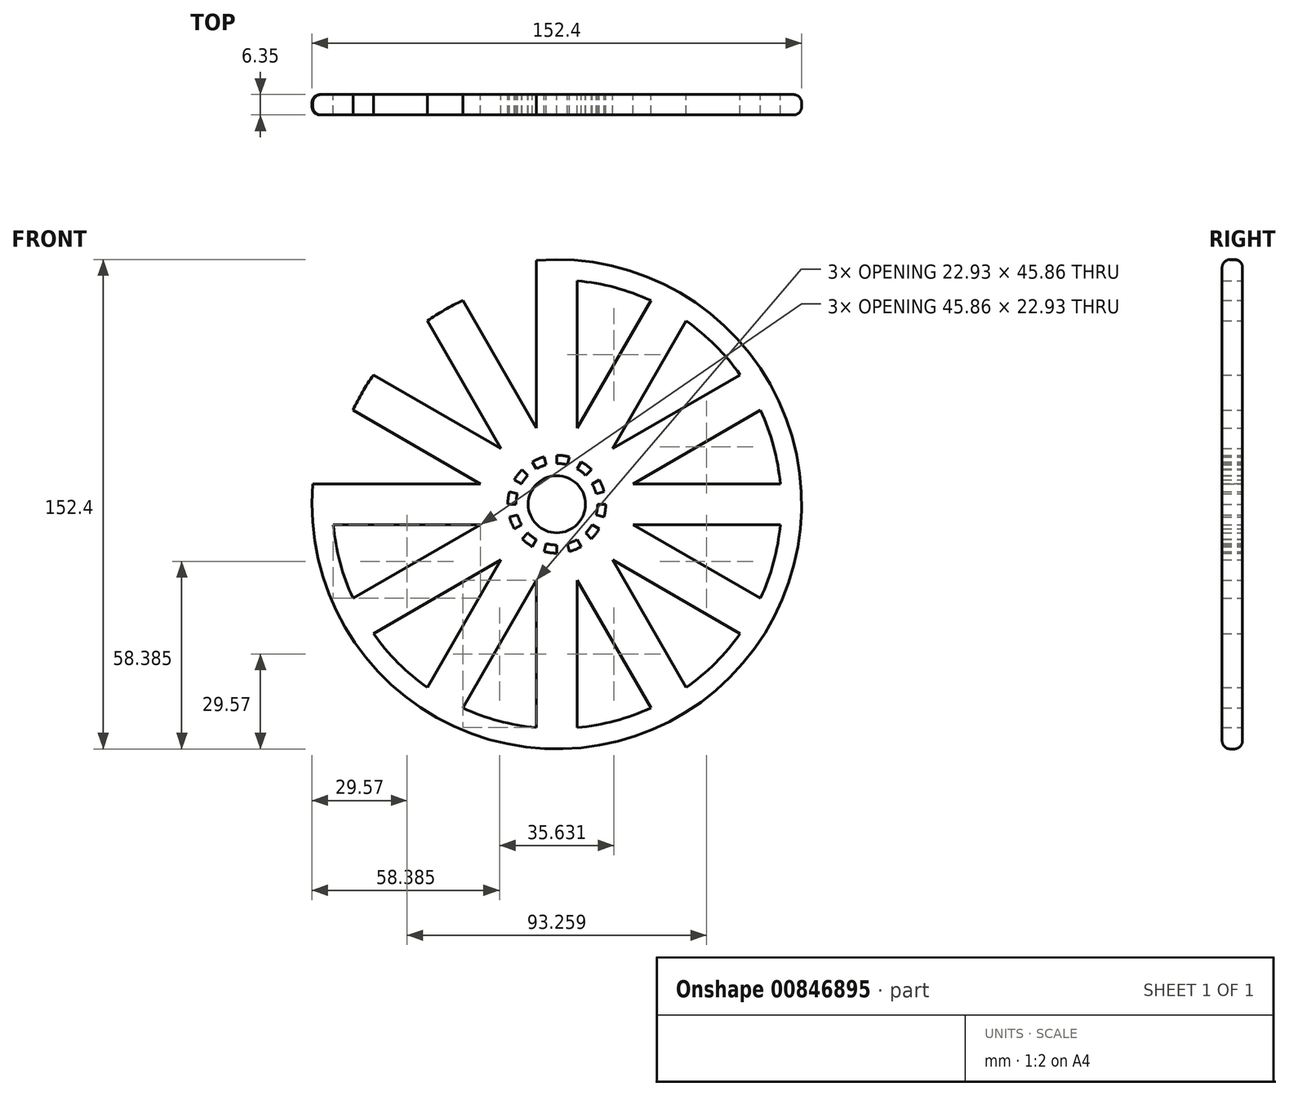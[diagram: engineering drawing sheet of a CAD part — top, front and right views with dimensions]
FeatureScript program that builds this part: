
annotation { "Feature Type Name" : "Feature", "Feature Type Description" : "" }
export const myFeature = defineFeature(function(context is Context, id is Id, definition is map)
    precondition{}
    {
        {
            var Q0;
            Q0=qCreatedBy(makeId("Front.planeOp"),FACE);
            var sketch = newSketch(context, id + "F0", { "sketchPlane" : qUnion([Q0])});
            skCircle(sketch, "E0", {"center": v(0, 0) * mm, "radius": 76.2 * mm});
            skLineSegment(sketch, "E1", {"start": v(-76.2, 0) * mm, "end": v(0, 0) * mm});
            skLineSegment(sketch, "E2", {"start": v(0, 0) * mm, "end": v(76.2, 0) * mm});
            skLineSegment(sketch, "E3", {"start": v(76.2, 0) * mm, "end": v(0, 0) * mm});
            skLineSegment(sketch, "E4", {"start": v(0, 0) * mm, "end": v(0, 76.2) * mm});
            skLineSegment(sketch, "E5", {"start": v(0, 76.2) * mm, "end": v(0, 0) * mm});
            skLineSegment(sketch, "E6", {"start": v(0, 0) * mm, "end": v(0, -76.2) * mm});
            skLineSegment(sketch, "E7", {"start": v(0, -76.2) * mm, "end": v(0, 0) * mm});
            skArc(sketch, "E8", {"start": v(-76.2, 0) * mm, "mid": v(-53.88, 53.88) * mm, "end": v(0, 76.2) * mm});
            skArc(sketch, "E9", {"start": v(76.2, 0) * mm, "mid": v(53.88, 53.88) * mm, "end": v(0, 76.2) * mm});
            skArc(sketch, "E10", {"start": v(-76.2, 0) * mm, "mid": v(-53.88, -53.88) * mm, "end": v(0, -76.2) * mm});
            skArc(sketch, "E11", {"start": v(0, -76.2) * mm, "mid": v(53.88, -53.88) * mm, "end": v(76.2, 0) * mm});
            skLineSegment(sketch, "E12", {"start": v(0, 0) * mm, "end": v(0, 6.35) * mm});
            skLineSegment(sketch, "E13", {"start": v(0, 0) * mm, "end": v(-6.35, 0) * mm});
            skLineSegment(sketch, "E14", {"start": v(0, 0) * mm, "end": v(66, 38.1) * mm});
            skLineSegment(sketch, "E15", {"start": v(0, 0) * mm, "end": v(38.1, 66) * mm});
            skLineSegment(sketch, "E16.MirrorCS", {"start": v(0, 0) * mm, "end": v(-38.1, 66) * mm});
            skLineSegment(sketch, "E17.MirrorCS", {"start": v(0, 0) * mm, "end": v(-66, 38.1) * mm});
            skLineSegment(sketch, "E18.MirrorCS", {"start": v(0, 0) * mm, "end": v(-66, -38.1) * mm});
            skLineSegment(sketch, "E19.MirrorCS", {"start": v(0, 0) * mm, "end": v(-38.1, -66) * mm});
            skLineSegment(sketch, "E20.MirrorCS", {"start": v(0, 0) * mm, "end": v(38.1, -66) * mm});
            skLineSegment(sketch, "E21.MirrorCS", {"start": v(0, 0) * mm, "end": v(66, -38.1) * mm});
            skArc(sketch, "E22.0", {"start": v(-69.85, 0) * mm, "mid": v(-49.4, 49.4) * mm, "end": v(0, 69.85) * mm});
            skArc(sketch, "E23.MirrorCS", {"start": v(69.85, 0) * mm, "mid": v(49.4, 49.4) * mm, "end": v(0, 69.85) * mm});
            skArc(sketch, "E24.MirrorCS", {"start": v(-69.85, 0) * mm, "mid": v(-49.4, -49.4) * mm, "end": v(0, -69.85) * mm});
            skArc(sketch, "E25.MirrorCS", {"start": v(69.85, 0) * mm, "mid": v(49.4, -49.4) * mm, "end": v(0, -69.85) * mm});
            skLineSegment(sketch, "E26.0", {"start": v(-23.7, 6.35) * mm, "end": v(-69.17, 32.6) * mm});
            skLineSegment(sketch, "E26.1", {"start": v(-76.2, 6.35) * mm, "end": v(-23.7, 6.35) * mm});
            skLineSegment(sketch, "E27.0", {"start": v(-17.35, 17.35) * mm, "end": v(-62.82, 43.6) * mm});
            skLineSegment(sketch, "E27.1", {"start": v(-17.35, 17.35) * mm, "end": v(-43.6, 62.82) * mm});
            skLineSegment(sketch, "E28.0", {"start": v(-6.35, 23.7) * mm, "end": v(-32.6, 69.17) * mm});
            skLineSegment(sketch, "E28.1", {"start": v(-6.35, 76.2) * mm, "end": v(-6.35, 23.7) * mm});
            skLineSegment(sketch, "E29.0", {"start": v(6.35, 23.7) * mm, "end": v(32.6, 69.17) * mm});
            skLineSegment(sketch, "E29.1", {"start": v(6.35, 76.2) * mm, "end": v(6.35, 23.7) * mm});
            skLineSegment(sketch, "E30.0", {"start": v(17.35, 17.35) * mm, "end": v(43.6, 62.82) * mm});
            skLineSegment(sketch, "E30.1", {"start": v(17.35, 17.35) * mm, "end": v(62.82, 43.6) * mm});
            skLineSegment(sketch, "E31.0", {"start": v(23.7, 6.35) * mm, "end": v(69.17, 32.6) * mm});
            skLineSegment(sketch, "E31.1", {"start": v(76.2, 6.35) * mm, "end": v(23.7, 6.35) * mm});
            skLineSegment(sketch, "E32.0", {"start": v(23.7, -6.35) * mm, "end": v(69.17, -32.6) * mm});
            skLineSegment(sketch, "E32.1", {"start": v(76.2, -6.35) * mm, "end": v(23.7, -6.35) * mm});
            skLineSegment(sketch, "E33.0", {"start": v(17.35, -17.35) * mm, "end": v(62.82, -43.6) * mm});
            skLineSegment(sketch, "E33.1", {"start": v(17.35, -17.35) * mm, "end": v(43.6, -62.82) * mm});
            skLineSegment(sketch, "E34.0", {"start": v(6.35, -23.7) * mm, "end": v(32.6, -69.17) * mm});
            skLineSegment(sketch, "E34.1", {"start": v(6.35, -76.2) * mm, "end": v(6.35, -23.7) * mm});
            skLineSegment(sketch, "E35.0", {"start": v(-6.35, -23.7) * mm, "end": v(-32.6, -69.17) * mm});
            skLineSegment(sketch, "E35.1", {"start": v(-6.35, -76.2) * mm, "end": v(-6.35, -23.7) * mm});
            skLineSegment(sketch, "E36.0", {"start": v(-17.35, -17.35) * mm, "end": v(-43.6, -62.82) * mm});
            skLineSegment(sketch, "E36.1", {"start": v(-17.35, -17.35) * mm, "end": v(-62.82, -43.6) * mm});
            skLineSegment(sketch, "E37.0", {"start": v(-23.7, -6.35) * mm, "end": v(-69.17, -32.6) * mm});
            skLineSegment(sketch, "E37.1", {"start": v(-76.2, -6.35) * mm, "end": v(-23.7, -6.35) * mm});
            skCircle(sketch, "E38", {"center": v(0, 0) * mm, "radius": 12.7 * mm});
            skCircle(sketch, "E39", {"center": v(0, 0) * mm, "radius": 19.05 * mm});
            skCircle(sketch, "E40.0", {"center": v(0, 0) * mm, "radius": 15.24 * mm});
            skLineSegment(sketch, "E41", {"start": v(0, 0) * mm, "end": v(23.7, 6.35) * mm});
            skLineSegment(sketch, "E42", {"start": v(-23.7, -6.35) * mm, "end": v(0, 0) * mm});
            skLineSegment(sketch, "E43", {"start": v(6.35, -23.7) * mm, "end": v(-6.35, 23.7) * mm});
            skLineSegment(sketch, "E44", {"start": v(6.35, 23.7) * mm, "end": v(-6.35, -23.7) * mm});
            skLineSegment(sketch, "E45", {"start": v(-17.35, -17.35) * mm, "end": v(17.35, 17.35) * mm});
            skLineSegment(sketch, "E46", {"start": v(23.7, -6.35) * mm, "end": v(-23.7, 6.35) * mm});
            skLineSegment(sketch, "E47", {"start": v(-17.35, 17.35) * mm, "end": v(17.35, -17.35) * mm});
            skCircle(sketch, "E48", {"center": v(0, 0) * mm, "radius": 8.9 * mm});
            skSolve(sketch);
        }
        {
            var Q0;
            {var subQ0=sQuery(id+"F0.wireOp",EDGE,"E22.0");var subQ5=sQuery(id+"F0.wireOp",EDGE,"E26.1");var subQ7=makeQuery(id+"F0.imprint","INTERSECT",VERTEX,{"derivedFrom":[subQ0,subQ5]});Q0=makeQuery(id+"F0.imprint","IMPRINT",FACE,{"disambiguationData":[TD([[makeQuery(id+"F0.imprint","IMPRINT",EDGE,{"disambiguationData":[TD([[subQ7,1.0]])],"derivedFrom":subQ5}),-1.0]])]});}
            var Q1;
            {var subQ0=sQuery(id+"F0.wireOp",EDGE,"E27.0");var subQ1=sQuery(id+"F0.wireOp",EDGE,"E8");var subQ2=makeQuery(id+"F0.imprint","INTERSECT",VERTEX,{"derivedFrom":[subQ1,subQ0]});Q1=makeQuery(id+"F0.imprint","IMPRINT",FACE,{"disambiguationData":[TD([[makeQuery(id+"F0.imprint","IMPRINT",EDGE,{"disambiguationData":[TD([[subQ2,-1.0]])],"derivedFrom":subQ1}),-1.0]])]});}
            var Q2;
            {var subQ0=sQuery(id+"F0.wireOp",EDGE,"E27.1");var subQ1=sQuery(id+"F0.wireOp",EDGE,"E8");var subQ2=makeQuery(id+"F0.imprint","INTERSECT",VERTEX,{"derivedFrom":[subQ1,subQ0]});Q2=makeQuery(id+"F0.imprint","IMPRINT",FACE,{"disambiguationData":[TD([[makeQuery(id+"F0.imprint","IMPRINT",EDGE,{"disambiguationData":[TD([[subQ2,-1.0]])],"derivedFrom":subQ1}),-1.0]])]});}
            var Q3;
            {var subQ0=sQuery(id+"F0.wireOp",EDGE,"E15");var subQ1=sQuery(id+"F0.wireOp",EDGE,"E9");var subQ2=makeQuery(id+"F0.imprint","INTERSECT",VERTEX,{"derivedFrom":[subQ1,subQ0]});Q3=makeQuery(id+"F0.imprint","IMPRINT",FACE,{"disambiguationData":[TD([[makeQuery(id+"F0.imprint","IMPRINT",EDGE,{"disambiguationData":[TD([[subQ2,-1.0]])],"derivedFrom":subQ1}),1.0]])]});}
            var Q4;
            {var subQ0=sQuery(id+"F0.wireOp",EDGE,"E39");var subQ1=sQuery(id+"F0.wireOp",EDGE,"E19.MirrorCS");var subQ2=makeQuery(id+"F0.imprint","INTERSECT",VERTEX,{"derivedFrom":[subQ1,subQ0]});Q4=makeQuery(id+"F0.imprint","IMPRINT",FACE,{"disambiguationData":[TD([[makeQuery(id+"F0.imprint","IMPRINT",EDGE,{"disambiguationData":[TD([[subQ2,-1.0]])],"derivedFrom":subQ1}),1.0]])]});}
            var Q5;
            {var subQ0=sQuery(id+"F0.wireOp",EDGE,"E39");var subQ1=sQuery(id+"F0.wireOp",EDGE,"E14");var subQ2=makeQuery(id+"F0.imprint","INTERSECT",VERTEX,{"derivedFrom":[subQ1,subQ0]});Q5=makeQuery(id+"F0.imprint","IMPRINT",FACE,{"disambiguationData":[TD([[makeQuery(id+"F0.imprint","IMPRINT",EDGE,{"disambiguationData":[TD([[subQ2,-1.0]])],"derivedFrom":subQ1}),-1.0]])]});}
            var Q6;
            {var subQ3=sQuery(id+"F0.wireOp",EDGE,"E23.MirrorCS");var subQ5=sQuery(id+"F0.wireOp",EDGE,"E31.1");var subQ6=makeQuery(id+"F0.imprint","INTERSECT",VERTEX,{"derivedFrom":[subQ3,subQ5]});Q6=makeQuery(id+"F0.imprint","IMPRINT",FACE,{"disambiguationData":[TD([[makeQuery(id+"F0.imprint","IMPRINT",EDGE,{"disambiguationData":[TD([[subQ6,1.0]])],"derivedFrom":subQ5}),1.0]])]});}
            var Q7;
            {var subQ0=sQuery(id+"F0.wireOp",EDGE,"E34.0");var subQ1=sQuery(id+"F0.wireOp",EDGE,"E11");var subQ2=makeQuery(id+"F0.imprint","INTERSECT",VERTEX,{"derivedFrom":[subQ1,subQ0]});Q7=makeQuery(id+"F0.imprint","IMPRINT",FACE,{"disambiguationData":[TD([[makeQuery(id+"F0.imprint","IMPRINT",EDGE,{"disambiguationData":[TD([[subQ2,-1.0]])],"derivedFrom":subQ1}),1.0]])]});}
            var Q8;
            {var subQ0=sQuery(id+"F0.wireOp",EDGE,"E26.1");var subQ1=sQuery(id+"F0.wireOp",EDGE,"E8");var subQ2=makeQuery(id+"F0.imprint","INTERSECT",VERTEX,{"derivedFrom":[subQ1,subQ0]});Q8=makeQuery(id+"F0.imprint","IMPRINT",FACE,{"disambiguationData":[TD([[makeQuery(id+"F0.imprint","IMPRINT",EDGE,{"disambiguationData":[TD([[subQ2,-1.0]])],"derivedFrom":subQ1}),-1.0]])]});}
            var Q9;
            {var subQ0=sQuery(id+"F0.wireOp",EDGE,"E20.MirrorCS");var subQ1=sQuery(id+"F0.wireOp",EDGE,"E11");var subQ2=makeQuery(id+"F0.imprint","INTERSECT",VERTEX,{"derivedFrom":[subQ1,subQ0]});Q9=makeQuery(id+"F0.imprint","IMPRINT",FACE,{"disambiguationData":[TD([[makeQuery(id+"F0.imprint","IMPRINT",EDGE,{"disambiguationData":[TD([[subQ2,-1.0]])],"derivedFrom":subQ1}),1.0]])]});}
            var Q10;
            {var subQ0=sQuery(id+"F0.wireOp",EDGE,"E30.0");var subQ1=sQuery(id+"F0.wireOp",EDGE,"E9");var subQ2=makeQuery(id+"F0.imprint","INTERSECT",VERTEX,{"derivedFrom":[subQ1,subQ0]});Q10=makeQuery(id+"F0.imprint","IMPRINT",FACE,{"disambiguationData":[TD([[makeQuery(id+"F0.imprint","IMPRINT",EDGE,{"disambiguationData":[TD([[subQ2,-1.0]])],"derivedFrom":subQ1}),1.0]])]});}
            var Q11;
            {var subQ0=sQuery(id+"F0.wireOp",EDGE,"E32.1");var subQ1=sQuery(id+"F0.wireOp",EDGE,"E11");var subQ2=makeQuery(id+"F0.imprint","INTERSECT",VERTEX,{"derivedFrom":[subQ1,subQ0]});Q11=makeQuery(id+"F0.imprint","IMPRINT",FACE,{"disambiguationData":[TD([[makeQuery(id+"F0.imprint","IMPRINT",EDGE,{"disambiguationData":[TD([[subQ2,1.0]])],"derivedFrom":subQ1}),1.0]])]});}
            var Q12;
            {var subQ0=sQuery(id+"F0.wireOp",EDGE,"E24.MirrorCS");var subQ5=sQuery(id+"F0.wireOp",EDGE,"E37.1");var subQ7=makeQuery(id+"F0.imprint","INTERSECT",VERTEX,{"derivedFrom":[subQ0,subQ5]});Q12=makeQuery(id+"F0.imprint","IMPRINT",FACE,{"disambiguationData":[TD([[makeQuery(id+"F0.imprint","IMPRINT",EDGE,{"disambiguationData":[TD([[subQ7,1.0]])],"derivedFrom":subQ5}),1.0]])]});}
            var Q13;
            {var subQ0=sQuery(id+"F0.wireOp",EDGE,"E18.MirrorCS");var subQ1=sQuery(id+"F0.wireOp",EDGE,"E10");var subQ2=makeQuery(id+"F0.imprint","INTERSECT",VERTEX,{"derivedFrom":[subQ1,subQ0]});Q13=makeQuery(id+"F0.imprint","IMPRINT",FACE,{"disambiguationData":[TD([[makeQuery(id+"F0.imprint","IMPRINT",EDGE,{"disambiguationData":[TD([[subQ2,-1.0]])],"derivedFrom":subQ1}),1.0]])]});}
            var Q14;
            {var subQ0=sQuery(id+"F0.wireOp",EDGE,"E39");var subQ1=sQuery(id+"F0.wireOp",EDGE,"E14");var subQ2=makeQuery(id+"F0.imprint","INTERSECT",VERTEX,{"derivedFrom":[subQ1,subQ0]});Q14=makeQuery(id+"F0.imprint","IMPRINT",FACE,{"disambiguationData":[TD([[makeQuery(id+"F0.imprint","IMPRINT",EDGE,{"disambiguationData":[TD([[subQ2,-1.0]])],"derivedFrom":subQ1}),1.0]])]});}
            var Q15;
            {var subQ0=sQuery(id+"F0.wireOp",EDGE,"E14");var subQ1=sQuery(id+"F0.wireOp",EDGE,"E9");var subQ2=makeQuery(id+"F0.imprint","INTERSECT",VERTEX,{"derivedFrom":[subQ1,subQ0]});Q15=makeQuery(id+"F0.imprint","IMPRINT",FACE,{"disambiguationData":[TD([[makeQuery(id+"F0.imprint","IMPRINT",EDGE,{"disambiguationData":[TD([[subQ2,-1.0]])],"derivedFrom":subQ1}),1.0]])]});}
            var Q16;
            {var subQ0=sQuery(id+"F0.wireOp",EDGE,"E36.0");var subQ1=sQuery(id+"F0.wireOp",EDGE,"E10");var subQ2=makeQuery(id+"F0.imprint","INTERSECT",VERTEX,{"derivedFrom":[subQ1,subQ0]});Q16=makeQuery(id+"F0.imprint","IMPRINT",FACE,{"disambiguationData":[TD([[makeQuery(id+"F0.imprint","IMPRINT",EDGE,{"disambiguationData":[TD([[subQ2,-1.0]])],"derivedFrom":subQ1}),1.0]])]});}
            var Q17;
            {var subQ0=sQuery(id+"F0.wireOp",EDGE,"E36.1");var subQ1=sQuery(id+"F0.wireOp",EDGE,"E10");var subQ2=makeQuery(id+"F0.imprint","INTERSECT",VERTEX,{"derivedFrom":[subQ1,subQ0]});Q17=makeQuery(id+"F0.imprint","IMPRINT",FACE,{"disambiguationData":[TD([[makeQuery(id+"F0.imprint","IMPRINT",EDGE,{"disambiguationData":[TD([[subQ2,-1.0]])],"derivedFrom":subQ1}),1.0]])]});}
            var Q18;
            {var subQ0=sQuery(id+"F0.wireOp",EDGE,"E39");var subQ1=sQuery(id+"F0.wireOp",EDGE,"E21.MirrorCS");var subQ2=makeQuery(id+"F0.imprint","INTERSECT",VERTEX,{"derivedFrom":[subQ1,subQ0]});Q18=makeQuery(id+"F0.imprint","IMPRINT",FACE,{"disambiguationData":[TD([[makeQuery(id+"F0.imprint","IMPRINT",EDGE,{"disambiguationData":[TD([[subQ2,-1.0]])],"derivedFrom":subQ1}),1.0]])]});}
            var Q19;
            {var subQ0=sQuery(id+"F0.wireOp",EDGE,"E33.1");var subQ1=sQuery(id+"F0.wireOp",EDGE,"E11");var subQ2=makeQuery(id+"F0.imprint","INTERSECT",VERTEX,{"derivedFrom":[subQ1,subQ0]});Q19=makeQuery(id+"F0.imprint","IMPRINT",FACE,{"disambiguationData":[TD([[makeQuery(id+"F0.imprint","IMPRINT",EDGE,{"disambiguationData":[TD([[subQ2,-1.0]])],"derivedFrom":subQ1}),1.0]])]});}
            var Q20;
            {var subQ0=sQuery(id+"F0.wireOp",EDGE,"E31.1");var subQ1=sQuery(id+"F0.wireOp",EDGE,"E9");var subQ2=makeQuery(id+"F0.imprint","INTERSECT",VERTEX,{"derivedFrom":[subQ1,subQ0]});Q20=makeQuery(id+"F0.imprint","IMPRINT",FACE,{"disambiguationData":[TD([[makeQuery(id+"F0.imprint","IMPRINT",EDGE,{"disambiguationData":[TD([[subQ2,-1.0]])],"derivedFrom":subQ1}),1.0]])]});}
            var Q21;
            {var subQ0=sQuery(id+"F0.wireOp",EDGE,"E39");var subQ1=sQuery(id+"F0.wireOp",EDGE,"E20.MirrorCS");var subQ2=makeQuery(id+"F0.imprint","INTERSECT",VERTEX,{"derivedFrom":[subQ1,subQ0]});Q21=makeQuery(id+"F0.imprint","IMPRINT",FACE,{"disambiguationData":[TD([[makeQuery(id+"F0.imprint","IMPRINT",EDGE,{"disambiguationData":[TD([[subQ2,-1.0]])],"derivedFrom":subQ1}),1.0]])]});}
            var Q22;
            {var subQ3=sQuery(id+"F0.wireOp",EDGE,"E23.MirrorCS");var subQ5=sQuery(id+"F0.wireOp",EDGE,"E29.1");var subQ7=makeQuery(id+"F0.imprint","INTERSECT",VERTEX,{"derivedFrom":[subQ3,subQ5]});Q22=makeQuery(id+"F0.imprint","IMPRINT",FACE,{"disambiguationData":[TD([[makeQuery(id+"F0.imprint","IMPRINT",EDGE,{"disambiguationData":[TD([[subQ7,1.0]])],"derivedFrom":subQ5}),-1.0]])]});}
            var Q23;
            {var subQ0=sQuery(id+"F0.wireOp",EDGE,"E29.1");var subQ1=sQuery(id+"F0.wireOp",EDGE,"E9");var subQ2=makeQuery(id+"F0.imprint","INTERSECT",VERTEX,{"derivedFrom":[subQ1,subQ0]});Q23=makeQuery(id+"F0.imprint","IMPRINT",FACE,{"disambiguationData":[TD([[makeQuery(id+"F0.imprint","IMPRINT",EDGE,{"disambiguationData":[TD([[subQ2,1.0]])],"derivedFrom":subQ1}),1.0]])]});}
            var Q24;
            {var subQ0=sQuery(id+"F0.wireOp",EDGE,"E28.1");var subQ1=sQuery(id+"F0.wireOp",EDGE,"E8");var subQ2=makeQuery(id+"F0.imprint","INTERSECT",VERTEX,{"derivedFrom":[subQ1,subQ0]});Q24=makeQuery(id+"F0.imprint","IMPRINT",FACE,{"disambiguationData":[TD([[makeQuery(id+"F0.imprint","IMPRINT",EDGE,{"disambiguationData":[TD([[subQ2,1.0]])],"derivedFrom":subQ1}),-1.0]])]});}
            var Q25;
            {var subQ3=sQuery(id+"F0.wireOp",EDGE,"E25.MirrorCS");var subQ5=sQuery(id+"F0.wireOp",EDGE,"E34.1");var subQ7=makeQuery(id+"F0.imprint","INTERSECT",VERTEX,{"derivedFrom":[subQ3,subQ5]});Q25=makeQuery(id+"F0.imprint","IMPRINT",FACE,{"disambiguationData":[TD([[makeQuery(id+"F0.imprint","IMPRINT",EDGE,{"disambiguationData":[TD([[subQ7,1.0]])],"derivedFrom":subQ5}),1.0]])]});}
            var Q26;
            {var subQ3=sQuery(id+"F0.wireOp",EDGE,"E22.0");var subQ5=sQuery(id+"F0.wireOp",EDGE,"E28.1");var subQ7=makeQuery(id+"F0.imprint","INTERSECT",VERTEX,{"derivedFrom":[subQ3,subQ5]});Q26=makeQuery(id+"F0.imprint","IMPRINT",FACE,{"disambiguationData":[TD([[makeQuery(id+"F0.imprint","IMPRINT",EDGE,{"disambiguationData":[TD([[subQ7,1.0]])],"derivedFrom":subQ5}),1.0]])]});}
            var Q27;
            {var subQ0=sQuery(id+"F0.wireOp",EDGE,"E34.1");var subQ1=sQuery(id+"F0.wireOp",EDGE,"E11");var subQ2=makeQuery(id+"F0.imprint","INTERSECT",VERTEX,{"derivedFrom":[subQ1,subQ0]});Q27=makeQuery(id+"F0.imprint","IMPRINT",FACE,{"disambiguationData":[TD([[makeQuery(id+"F0.imprint","IMPRINT",EDGE,{"disambiguationData":[TD([[subQ2,-1.0]])],"derivedFrom":subQ1}),1.0]])]});}
            var Q28;
            {var subQ0=sQuery(id+"F0.wireOp",EDGE,"E39");var subQ1=sQuery(id+"F0.wireOp",EDGE,"E18.MirrorCS");var subQ2=makeQuery(id+"F0.imprint","INTERSECT",VERTEX,{"derivedFrom":[subQ1,subQ0]});Q28=makeQuery(id+"F0.imprint","IMPRINT",FACE,{"disambiguationData":[TD([[makeQuery(id+"F0.imprint","IMPRINT",EDGE,{"disambiguationData":[TD([[subQ2,-1.0]])],"derivedFrom":subQ1}),1.0]])]});}
            var Q29;
            {var subQ0=sQuery(id+"F0.wireOp",EDGE,"E16.MirrorCS");var subQ1=sQuery(id+"F0.wireOp",EDGE,"E8");var subQ2=makeQuery(id+"F0.imprint","INTERSECT",VERTEX,{"derivedFrom":[subQ1,subQ0]});Q29=makeQuery(id+"F0.imprint","IMPRINT",FACE,{"disambiguationData":[TD([[makeQuery(id+"F0.imprint","IMPRINT",EDGE,{"disambiguationData":[TD([[subQ2,-1.0]])],"derivedFrom":subQ1}),-1.0]])]});}
            var Q30;
            {var subQ3=sQuery(id+"F0.wireOp",EDGE,"E24.MirrorCS");var subQ5=sQuery(id+"F0.wireOp",EDGE,"E35.1");var subQ7=makeQuery(id+"F0.imprint","INTERSECT",VERTEX,{"derivedFrom":[subQ3,subQ5]});Q30=makeQuery(id+"F0.imprint","IMPRINT",FACE,{"disambiguationData":[TD([[makeQuery(id+"F0.imprint","IMPRINT",EDGE,{"disambiguationData":[TD([[subQ7,1.0]])],"derivedFrom":subQ5}),-1.0]])]});}
            var Q31;
            {var subQ0=sQuery(id+"F0.wireOp",EDGE,"E31.0");var subQ1=sQuery(id+"F0.wireOp",EDGE,"E9");var subQ2=makeQuery(id+"F0.imprint","INTERSECT",VERTEX,{"derivedFrom":[subQ1,subQ0]});Q31=makeQuery(id+"F0.imprint","IMPRINT",FACE,{"disambiguationData":[TD([[makeQuery(id+"F0.imprint","IMPRINT",EDGE,{"disambiguationData":[TD([[subQ2,-1.0]])],"derivedFrom":subQ1}),1.0]])]});}
            var Q32;
            {var subQ3=sQuery(id+"F0.wireOp",EDGE,"E25.MirrorCS");var subQ5=sQuery(id+"F0.wireOp",EDGE,"E32.1");var subQ7=makeQuery(id+"F0.imprint","INTERSECT",VERTEX,{"derivedFrom":[subQ3,subQ5]});Q32=makeQuery(id+"F0.imprint","IMPRINT",FACE,{"disambiguationData":[TD([[makeQuery(id+"F0.imprint","IMPRINT",EDGE,{"disambiguationData":[TD([[subQ7,1.0]])],"derivedFrom":subQ5}),-1.0]])]});}
            var Q33;
            {var subQ0=sQuery(id+"F0.wireOp",EDGE,"E19.MirrorCS");var subQ1=sQuery(id+"F0.wireOp",EDGE,"E10");var subQ2=makeQuery(id+"F0.imprint","INTERSECT",VERTEX,{"derivedFrom":[subQ1,subQ0]});Q33=makeQuery(id+"F0.imprint","IMPRINT",FACE,{"disambiguationData":[TD([[makeQuery(id+"F0.imprint","IMPRINT",EDGE,{"disambiguationData":[TD([[subQ2,-1.0]])],"derivedFrom":subQ1}),1.0]])]});}
            var Q34;
            {var subQ0=sQuery(id+"F0.wireOp",EDGE,"E39");var subQ1=sQuery(id+"F0.wireOp",EDGE,"E16.MirrorCS");var subQ2=makeQuery(id+"F0.imprint","INTERSECT",VERTEX,{"derivedFrom":[subQ1,subQ0]});Q34=makeQuery(id+"F0.imprint","IMPRINT",FACE,{"disambiguationData":[TD([[makeQuery(id+"F0.imprint","IMPRINT",EDGE,{"disambiguationData":[TD([[subQ2,-1.0]])],"derivedFrom":subQ1}),1.0]])]});}
            var Q35;
            {var subQ0=sQuery(id+"F0.wireOp",EDGE,"E26.0");var subQ1=sQuery(id+"F0.wireOp",EDGE,"E8");var subQ2=makeQuery(id+"F0.imprint","INTERSECT",VERTEX,{"derivedFrom":[subQ1,subQ0]});Q35=makeQuery(id+"F0.imprint","IMPRINT",FACE,{"disambiguationData":[TD([[makeQuery(id+"F0.imprint","IMPRINT",EDGE,{"disambiguationData":[TD([[subQ2,-1.0]])],"derivedFrom":subQ1}),-1.0]])]});}
            var Q36;
            {var subQ0=sQuery(id+"F0.wireOp",EDGE,"E21.MirrorCS");var subQ1=sQuery(id+"F0.wireOp",EDGE,"E11");var subQ2=makeQuery(id+"F0.imprint","INTERSECT",VERTEX,{"derivedFrom":[subQ1,subQ0]});Q36=makeQuery(id+"F0.imprint","IMPRINT",FACE,{"disambiguationData":[TD([[makeQuery(id+"F0.imprint","IMPRINT",EDGE,{"disambiguationData":[TD([[subQ2,-1.0]])],"derivedFrom":subQ1}),1.0]])]});}
            var Q37;
            {var subQ0=sQuery(id+"F0.wireOp",EDGE,"E17.MirrorCS");var subQ1=sQuery(id+"F0.wireOp",EDGE,"E8");var subQ2=makeQuery(id+"F0.imprint","INTERSECT",VERTEX,{"derivedFrom":[subQ1,subQ0]});Q37=makeQuery(id+"F0.imprint","IMPRINT",FACE,{"disambiguationData":[TD([[makeQuery(id+"F0.imprint","IMPRINT",EDGE,{"disambiguationData":[TD([[subQ2,-1.0]])],"derivedFrom":subQ1}),-1.0]])]});}
            var Q38;
            {var subQ0=sQuery(id+"F0.wireOp",EDGE,"E33.0");var subQ1=sQuery(id+"F0.wireOp",EDGE,"E11");var subQ2=makeQuery(id+"F0.imprint","INTERSECT",VERTEX,{"derivedFrom":[subQ1,subQ0]});Q38=makeQuery(id+"F0.imprint","IMPRINT",FACE,{"disambiguationData":[TD([[makeQuery(id+"F0.imprint","IMPRINT",EDGE,{"disambiguationData":[TD([[subQ2,-1.0]])],"derivedFrom":subQ1}),1.0]])]});}
            var Q39;
            {var subQ0=sQuery(id+"F0.wireOp",EDGE,"E39");var subQ1=sQuery(id+"F0.wireOp",EDGE,"E20.MirrorCS");var subQ2=makeQuery(id+"F0.imprint","INTERSECT",VERTEX,{"derivedFrom":[subQ1,subQ0]});Q39=makeQuery(id+"F0.imprint","IMPRINT",FACE,{"disambiguationData":[TD([[makeQuery(id+"F0.imprint","IMPRINT",EDGE,{"disambiguationData":[TD([[subQ2,-1.0]])],"derivedFrom":subQ1}),-1.0]])]});}
            var Q40;
            {var subQ0=sQuery(id+"F0.wireOp",EDGE,"E37.1");var subQ1=sQuery(id+"F0.wireOp",EDGE,"E10");var subQ2=makeQuery(id+"F0.imprint","INTERSECT",VERTEX,{"derivedFrom":[subQ1,subQ0]});Q40=makeQuery(id+"F0.imprint","IMPRINT",FACE,{"disambiguationData":[TD([[makeQuery(id+"F0.imprint","IMPRINT",EDGE,{"disambiguationData":[TD([[subQ2,-1.0]])],"derivedFrom":subQ1}),1.0]])]});}
            var Q41;
            {var subQ0=sQuery(id+"F0.wireOp",EDGE,"E37.0");var subQ1=sQuery(id+"F0.wireOp",EDGE,"E10");var subQ2=makeQuery(id+"F0.imprint","INTERSECT",VERTEX,{"derivedFrom":[subQ1,subQ0]});Q41=makeQuery(id+"F0.imprint","IMPRINT",FACE,{"disambiguationData":[TD([[makeQuery(id+"F0.imprint","IMPRINT",EDGE,{"disambiguationData":[TD([[subQ2,-1.0]])],"derivedFrom":subQ1}),1.0]])]});}
            var Q42;
            {var subQ0=sQuery(id+"F0.wireOp",EDGE,"E35.1");var subQ1=sQuery(id+"F0.wireOp",EDGE,"E10");var subQ2=makeQuery(id+"F0.imprint","INTERSECT",VERTEX,{"derivedFrom":[subQ1,subQ0]});Q42=makeQuery(id+"F0.imprint","IMPRINT",FACE,{"disambiguationData":[TD([[makeQuery(id+"F0.imprint","IMPRINT",EDGE,{"disambiguationData":[TD([[subQ2,1.0]])],"derivedFrom":subQ1}),1.0]])]});}
            var Q43;
            {var subQ0=sQuery(id+"F0.wireOp",EDGE,"E30.1");var subQ1=sQuery(id+"F0.wireOp",EDGE,"E9");var subQ2=makeQuery(id+"F0.imprint","INTERSECT",VERTEX,{"derivedFrom":[subQ1,subQ0]});Q43=makeQuery(id+"F0.imprint","IMPRINT",FACE,{"disambiguationData":[TD([[makeQuery(id+"F0.imprint","IMPRINT",EDGE,{"disambiguationData":[TD([[subQ2,-1.0]])],"derivedFrom":subQ1}),1.0]])]});}
            var Q44;
            {var subQ0=sQuery(id+"F0.wireOp",EDGE,"E38");var subQ1=sQuery(id+"F0.wireOp",EDGE,"E1");var subQ2=makeQuery(id+"F0.imprint","INTERSECT",VERTEX,{"derivedFrom":[subQ1,subQ0]});Q44=makeQuery(id+"F0.imprint","IMPRINT",FACE,{"disambiguationData":[TD([[makeQuery(id+"F0.imprint","IMPRINT",EDGE,{"disambiguationData":[TD([[subQ2,1.0]])],"derivedFrom":subQ1}),-1.0]])]});}
            var Q45;
            {var subQ0=sQuery(id+"F0.wireOp",EDGE,"E40.0");var subQ1=sQuery(id+"F0.wireOp",EDGE,"E4");var subQ2=makeQuery(id+"F0.imprint","INTERSECT",VERTEX,{"derivedFrom":[subQ1,subQ0]});Q45=makeQuery(id+"F0.imprint","IMPRINT",FACE,{"disambiguationData":[TD([[makeQuery(id+"F0.imprint","IMPRINT",EDGE,{"disambiguationData":[TD([[subQ2,1.0]])],"derivedFrom":subQ1}),1.0]])]});}
            var Q46;
            {var subQ0=sQuery(id+"F0.wireOp",EDGE,"E39");var subQ1=sQuery(id+"F0.wireOp",EDGE,"E16.MirrorCS");var subQ2=makeQuery(id+"F0.imprint","INTERSECT",VERTEX,{"derivedFrom":[subQ1,subQ0]});Q46=makeQuery(id+"F0.imprint","IMPRINT",FACE,{"disambiguationData":[TD([[makeQuery(id+"F0.imprint","IMPRINT",EDGE,{"disambiguationData":[TD([[subQ2,-1.0]])],"derivedFrom":subQ1}),-1.0]])]});}
            var Q47;
            {var subQ0=sQuery(id+"F0.wireOp",EDGE,"E39");var subQ1=sQuery(id+"F0.wireOp",EDGE,"E4");var subQ2=makeQuery(id+"F0.imprint","INTERSECT",VERTEX,{"derivedFrom":[subQ1,subQ0]});Q47=makeQuery(id+"F0.imprint","IMPRINT",FACE,{"disambiguationData":[TD([[makeQuery(id+"F0.imprint","IMPRINT",EDGE,{"disambiguationData":[TD([[subQ2,1.0]])],"derivedFrom":subQ1}),-1.0]])]});}
            var Q48;
            {var subQ1=sQuery(id+"F0.wireOp",EDGE,"E15");var subQ7=sQuery(id+"F0.wireOp",EDGE,"E39");var subQ8=makeQuery(id+"F0.imprint","INTERSECT",VERTEX,{"derivedFrom":[subQ1,subQ7]});Q48=makeQuery(id+"F0.imprint","IMPRINT",FACE,{"disambiguationData":[TD([[makeQuery(id+"F0.imprint","IMPRINT",EDGE,{"disambiguationData":[TD([[subQ8,-1.0]])],"derivedFrom":subQ1}),1.0]])]});}
            var Q49;
            {var subQ0=sQuery(id+"F0.wireOp",EDGE,"E39");var subQ1=sQuery(id+"F0.wireOp",EDGE,"E14");var subQ2=makeQuery(id+"F0.imprint","INTERSECT",VERTEX,{"derivedFrom":[subQ1,subQ0]});Q49=makeQuery(id+"F0.imprint","IMPRINT",FACE,{"disambiguationData":[TD([[makeQuery(id+"F0.imprint","IMPRINT",EDGE,{"disambiguationData":[TD([[subQ2,1.0]])],"derivedFrom":subQ1}),1.0]])]});}
            var Q50;
            {var subQ0=sQuery(id+"F0.wireOp",EDGE,"E39");var subQ1=sQuery(id+"F0.wireOp",EDGE,"E2");var subQ2=makeQuery(id+"F0.imprint","INTERSECT",VERTEX,{"derivedFrom":[subQ1,subQ0]});Q50=makeQuery(id+"F0.imprint","IMPRINT",FACE,{"disambiguationData":[TD([[makeQuery(id+"F0.imprint","IMPRINT",EDGE,{"disambiguationData":[TD([[subQ2,1.0]])],"derivedFrom":subQ1}),1.0]])]});}
            var Q51;
            {var subQ0=sQuery(id+"F0.wireOp",EDGE,"E39");var subQ1=sQuery(id+"F0.wireOp",EDGE,"E2");var subQ2=makeQuery(id+"F0.imprint","INTERSECT",VERTEX,{"derivedFrom":[subQ1,subQ0]});Q51=makeQuery(id+"F0.imprint","IMPRINT",FACE,{"disambiguationData":[TD([[makeQuery(id+"F0.imprint","IMPRINT",EDGE,{"disambiguationData":[TD([[subQ2,1.0]])],"derivedFrom":subQ1}),-1.0]])]});}
            var Q52;
            {var subQ0=sQuery(id+"F0.wireOp",EDGE,"E39");var subQ1=sQuery(id+"F0.wireOp",EDGE,"E20.MirrorCS");var subQ2=makeQuery(id+"F0.imprint","INTERSECT",VERTEX,{"derivedFrom":[subQ1,subQ0]});Q52=makeQuery(id+"F0.imprint","IMPRINT",FACE,{"disambiguationData":[TD([[makeQuery(id+"F0.imprint","IMPRINT",EDGE,{"disambiguationData":[TD([[subQ2,1.0]])],"derivedFrom":subQ1}),1.0]])]});}
            var Q53;
            {var subQ0=sQuery(id+"F0.wireOp",EDGE,"E39");var subQ1=sQuery(id+"F0.wireOp",EDGE,"E6");var subQ2=makeQuery(id+"F0.imprint","INTERSECT",VERTEX,{"derivedFrom":[subQ1,subQ0]});Q53=makeQuery(id+"F0.imprint","IMPRINT",FACE,{"disambiguationData":[TD([[makeQuery(id+"F0.imprint","IMPRINT",EDGE,{"disambiguationData":[TD([[subQ2,1.0]])],"derivedFrom":subQ1}),1.0]])]});}
            var Q54;
            {var subQ0=sQuery(id+"F0.wireOp",EDGE,"E39");var subQ1=sQuery(id+"F0.wireOp",EDGE,"E6");var subQ2=makeQuery(id+"F0.imprint","INTERSECT",VERTEX,{"derivedFrom":[subQ1,subQ0]});Q54=makeQuery(id+"F0.imprint","IMPRINT",FACE,{"disambiguationData":[TD([[makeQuery(id+"F0.imprint","IMPRINT",EDGE,{"disambiguationData":[TD([[subQ2,1.0]])],"derivedFrom":subQ1}),-1.0]])]});}
            var Q55;
            {var subQ0=sQuery(id+"F0.wireOp",EDGE,"E39");var subQ1=sQuery(id+"F0.wireOp",EDGE,"E1");var subQ2=makeQuery(id+"F0.imprint","INTERSECT",VERTEX,{"derivedFrom":[subQ1,subQ0]});Q55=makeQuery(id+"F0.imprint","IMPRINT",FACE,{"disambiguationData":[TD([[makeQuery(id+"F0.imprint","IMPRINT",EDGE,{"disambiguationData":[TD([[subQ2,-1.0]])],"derivedFrom":subQ1}),-1.0]])]});}
            var Q56;
            {var subQ0=sQuery(id+"F0.wireOp",EDGE,"E39");var subQ1=sQuery(id+"F0.wireOp",EDGE,"E16.MirrorCS");var subQ2=makeQuery(id+"F0.imprint","INTERSECT",VERTEX,{"derivedFrom":[subQ1,subQ0]});Q56=makeQuery(id+"F0.imprint","IMPRINT",FACE,{"disambiguationData":[TD([[makeQuery(id+"F0.imprint","IMPRINT",EDGE,{"disambiguationData":[TD([[subQ2,1.0]])],"derivedFrom":subQ1}),1.0]])]});}
            var Q57;
            {var subQ0=sQuery(id+"F0.wireOp",EDGE,"E39");var subQ1=sQuery(id+"F0.wireOp",EDGE,"E4");var subQ2=makeQuery(id+"F0.imprint","INTERSECT",VERTEX,{"derivedFrom":[subQ1,subQ0]});Q57=makeQuery(id+"F0.imprint","IMPRINT",FACE,{"disambiguationData":[TD([[makeQuery(id+"F0.imprint","IMPRINT",EDGE,{"disambiguationData":[TD([[subQ2,1.0]])],"derivedFrom":subQ1}),1.0]])]});}
            var Q58;
            {var subQ0=sQuery(id+"F0.wireOp",EDGE,"E48");var subQ1=sQuery(id+"F0.wireOp",EDGE,"E16.MirrorCS");var subQ2=makeQuery(id+"F0.imprint","INTERSECT",VERTEX,{"derivedFrom":[subQ1,subQ0]});Q58=makeQuery(id+"F0.imprint","IMPRINT",FACE,{"disambiguationData":[TD([[makeQuery(id+"F0.imprint","IMPRINT",EDGE,{"disambiguationData":[TD([[subQ2,-1.0]])],"derivedFrom":subQ1}),1.0]])]});}
            var Q59;
            {var subQ0=sQuery(id+"F0.wireOp",EDGE,"E48");var subQ1=sQuery(id+"F0.wireOp",EDGE,"E14");var subQ2=makeQuery(id+"F0.imprint","INTERSECT",VERTEX,{"derivedFrom":[subQ1,subQ0]});Q59=makeQuery(id+"F0.imprint","IMPRINT",FACE,{"disambiguationData":[TD([[makeQuery(id+"F0.imprint","IMPRINT",EDGE,{"disambiguationData":[TD([[subQ2,-1.0]])],"derivedFrom":subQ1}),1.0]])]});}
            var Q60;
            {var subQ0=sQuery(id+"F0.wireOp",EDGE,"E40.0");var subQ1=sQuery(id+"F0.wireOp",EDGE,"E14");var subQ2=makeQuery(id+"F0.imprint","INTERSECT",VERTEX,{"derivedFrom":[subQ1,subQ0]});Q60=makeQuery(id+"F0.imprint","IMPRINT",FACE,{"disambiguationData":[TD([[makeQuery(id+"F0.imprint","IMPRINT",EDGE,{"disambiguationData":[TD([[subQ2,1.0]])],"derivedFrom":subQ1}),1.0]])]});}
            var Q61;
            {var subQ0=sQuery(id+"F0.wireOp",EDGE,"E40.0");var subQ1=sQuery(id+"F0.wireOp",EDGE,"E2");var subQ2=makeQuery(id+"F0.imprint","INTERSECT",VERTEX,{"derivedFrom":[subQ1,subQ0]});Q61=makeQuery(id+"F0.imprint","IMPRINT",FACE,{"disambiguationData":[TD([[makeQuery(id+"F0.imprint","IMPRINT",EDGE,{"disambiguationData":[TD([[subQ2,1.0]])],"derivedFrom":subQ1}),1.0]])]});}
            var Q62;
            {var subQ0=sQuery(id+"F0.wireOp",EDGE,"E48");var subQ1=sQuery(id+"F0.wireOp",EDGE,"E2");var subQ2=makeQuery(id+"F0.imprint","INTERSECT",VERTEX,{"derivedFrom":[subQ1,subQ0]});Q62=makeQuery(id+"F0.imprint","IMPRINT",FACE,{"disambiguationData":[TD([[makeQuery(id+"F0.imprint","IMPRINT",EDGE,{"disambiguationData":[TD([[subQ2,-1.0]])],"derivedFrom":subQ1}),1.0]])]});}
            var Q63;
            {var subQ0=sQuery(id+"F0.wireOp",EDGE,"E48");var subQ1=sQuery(id+"F0.wireOp",EDGE,"E2");var subQ2=makeQuery(id+"F0.imprint","INTERSECT",VERTEX,{"derivedFrom":[subQ1,subQ0]});Q63=makeQuery(id+"F0.imprint","IMPRINT",FACE,{"disambiguationData":[TD([[makeQuery(id+"F0.imprint","IMPRINT",EDGE,{"disambiguationData":[TD([[subQ2,-1.0]])],"derivedFrom":subQ1}),-1.0]])]});}
            var Q64;
            {var subQ0=sQuery(id+"F0.wireOp",EDGE,"E40.0");var subQ1=sQuery(id+"F0.wireOp",EDGE,"E20.MirrorCS");var subQ2=makeQuery(id+"F0.imprint","INTERSECT",VERTEX,{"derivedFrom":[subQ1,subQ0]});Q64=makeQuery(id+"F0.imprint","IMPRINT",FACE,{"disambiguationData":[TD([[makeQuery(id+"F0.imprint","IMPRINT",EDGE,{"disambiguationData":[TD([[subQ2,1.0]])],"derivedFrom":subQ1}),1.0]])]});}
            var Q65;
            {var subQ0=sQuery(id+"F0.wireOp",EDGE,"E48");var subQ1=sQuery(id+"F0.wireOp",EDGE,"E20.MirrorCS");var subQ2=makeQuery(id+"F0.imprint","INTERSECT",VERTEX,{"derivedFrom":[subQ1,subQ0]});Q65=makeQuery(id+"F0.imprint","IMPRINT",FACE,{"disambiguationData":[TD([[makeQuery(id+"F0.imprint","IMPRINT",EDGE,{"disambiguationData":[TD([[subQ2,-1.0]])],"derivedFrom":subQ1}),1.0]])]});}
            var Q66;
            {var subQ0=sQuery(id+"F0.wireOp",EDGE,"E40.0");var subQ1=sQuery(id+"F0.wireOp",EDGE,"E6");var subQ2=makeQuery(id+"F0.imprint","INTERSECT",VERTEX,{"derivedFrom":[subQ1,subQ0]});Q66=makeQuery(id+"F0.imprint","IMPRINT",FACE,{"disambiguationData":[TD([[makeQuery(id+"F0.imprint","IMPRINT",EDGE,{"disambiguationData":[TD([[subQ2,1.0]])],"derivedFrom":subQ1}),1.0]])]});}
            var Q67;
            {var subQ0=sQuery(id+"F0.wireOp",EDGE,"E48");var subQ1=sQuery(id+"F0.wireOp",EDGE,"E6");var subQ2=makeQuery(id+"F0.imprint","INTERSECT",VERTEX,{"derivedFrom":[subQ1,subQ0]});Q67=makeQuery(id+"F0.imprint","IMPRINT",FACE,{"disambiguationData":[TD([[makeQuery(id+"F0.imprint","IMPRINT",EDGE,{"disambiguationData":[TD([[subQ2,-1.0]])],"derivedFrom":subQ1}),-1.0]])]});}
            var Q68;
            {var subQ0=sQuery(id+"F0.wireOp",EDGE,"E40.0");var subQ1=sQuery(id+"F0.wireOp",EDGE,"E18.MirrorCS");var subQ2=makeQuery(id+"F0.imprint","INTERSECT",VERTEX,{"derivedFrom":[subQ1,subQ0]});Q68=makeQuery(id+"F0.imprint","IMPRINT",FACE,{"disambiguationData":[TD([[makeQuery(id+"F0.imprint","IMPRINT",EDGE,{"disambiguationData":[TD([[subQ2,1.0]])],"derivedFrom":subQ1}),1.0]])]});}
            var Q69;
            {var subQ0=sQuery(id+"F0.wireOp",EDGE,"E48");var subQ1=sQuery(id+"F0.wireOp",EDGE,"E18.MirrorCS");var subQ2=makeQuery(id+"F0.imprint","INTERSECT",VERTEX,{"derivedFrom":[subQ1,subQ0]});Q69=makeQuery(id+"F0.imprint","IMPRINT",FACE,{"disambiguationData":[TD([[makeQuery(id+"F0.imprint","IMPRINT",EDGE,{"disambiguationData":[TD([[subQ2,-1.0]])],"derivedFrom":subQ1}),1.0]])]});}
            var Q70;
            {var subQ0=sQuery(id+"F0.wireOp",EDGE,"E48");var subQ1=sQuery(id+"F0.wireOp",EDGE,"E6");var subQ2=makeQuery(id+"F0.imprint","INTERSECT",VERTEX,{"derivedFrom":[subQ1,subQ0]});Q70=makeQuery(id+"F0.imprint","IMPRINT",FACE,{"disambiguationData":[TD([[makeQuery(id+"F0.imprint","IMPRINT",EDGE,{"disambiguationData":[TD([[subQ2,-1.0]])],"derivedFrom":subQ1}),1.0]])]});}
            var Q71;
            {var subQ0=sQuery(id+"F0.wireOp",EDGE,"E40.0");var subQ1=sQuery(id+"F0.wireOp",EDGE,"E16.MirrorCS");var subQ2=makeQuery(id+"F0.imprint","INTERSECT",VERTEX,{"derivedFrom":[subQ1,subQ0]});Q71=makeQuery(id+"F0.imprint","IMPRINT",FACE,{"disambiguationData":[TD([[makeQuery(id+"F0.imprint","IMPRINT",EDGE,{"disambiguationData":[TD([[subQ2,1.0]])],"derivedFrom":subQ1}),1.0]])]});}
            var Q72;
            {var subQ0=sQuery(id+"F0.wireOp",EDGE,"E39");var subQ1=sQuery(id+"F0.wireOp",EDGE,"E1");var subQ2=makeQuery(id+"F0.imprint","INTERSECT",VERTEX,{"derivedFrom":[subQ1,subQ0]});Q72=makeQuery(id+"F0.imprint","IMPRINT",FACE,{"disambiguationData":[TD([[makeQuery(id+"F0.imprint","IMPRINT",EDGE,{"disambiguationData":[TD([[subQ2,-1.0]])],"derivedFrom":subQ1}),1.0]])]});}
            var Q73;
            {var subQ0=sQuery(id+"F0.wireOp",EDGE,"E39");var subQ1=sQuery(id+"F0.wireOp",EDGE,"E18.MirrorCS");var subQ2=makeQuery(id+"F0.imprint","INTERSECT",VERTEX,{"derivedFrom":[subQ1,subQ0]});Q73=makeQuery(id+"F0.imprint","IMPRINT",FACE,{"disambiguationData":[TD([[makeQuery(id+"F0.imprint","IMPRINT",EDGE,{"disambiguationData":[TD([[subQ2,1.0]])],"derivedFrom":subQ1}),1.0]])]});}
            var Q74;
            {var subQ0=sQuery(id+"F0.wireOp",EDGE,"E39");var subQ1=sQuery(id+"F0.wireOp",EDGE,"E18.MirrorCS");var subQ2=makeQuery(id+"F0.imprint","INTERSECT",VERTEX,{"derivedFrom":[subQ1,subQ0]});Q74=makeQuery(id+"F0.imprint","IMPRINT",FACE,{"disambiguationData":[TD([[makeQuery(id+"F0.imprint","IMPRINT",EDGE,{"disambiguationData":[TD([[subQ2,-1.0]])],"derivedFrom":subQ1}),-1.0]])]});}
            var Q75;
            {var subQ0=sQuery(id+"F0.wireOp",EDGE,"E39");var subQ1=sQuery(id+"F0.wireOp",EDGE,"E17.MirrorCS");var subQ2=makeQuery(id+"F0.imprint","INTERSECT",VERTEX,{"derivedFrom":[subQ1,subQ0]});Q75=makeQuery(id+"F0.imprint","IMPRINT",FACE,{"disambiguationData":[TD([[makeQuery(id+"F0.imprint","IMPRINT",EDGE,{"disambiguationData":[TD([[subQ2,-1.0]])],"derivedFrom":subQ1}),1.0]])]});}
            var Q76;
            {var subQ5=sQuery(id+"F0.wireOp",EDGE,"E39");var subQ7=sQuery(id+"F0.wireOp",EDGE,"E2");var subQ8=makeQuery(id+"F0.imprint","INTERSECT",VERTEX,{"derivedFrom":[subQ7,subQ5]});Q76=makeQuery(id+"F0.imprint","IMPRINT",FACE,{"disambiguationData":[TD([[makeQuery(id+"F0.imprint","IMPRINT",EDGE,{"disambiguationData":[TD([[subQ8,-1.0]])],"derivedFrom":subQ5}),-1.0]])]});}
            var Q77;
            {var subQ0=sQuery(id+"F0.wireOp",EDGE,"E39");var subQ1=sQuery(id+"F0.wireOp",EDGE,"E2");var subQ2=makeQuery(id+"F0.imprint","INTERSECT",VERTEX,{"derivedFrom":[subQ1,subQ0]});Q77=makeQuery(id+"F0.imprint","IMPRINT",FACE,{"disambiguationData":[TD([[makeQuery(id+"F0.imprint","IMPRINT",EDGE,{"disambiguationData":[TD([[subQ2,1.0]])],"derivedFrom":subQ0}),-1.0]])]});}
            var Q78;
            {var subQ0=sQuery(id+"F0.wireOp",EDGE,"E39");var subQ1=sQuery(id+"F0.wireOp",EDGE,"E21.MirrorCS");var subQ2=makeQuery(id+"F0.imprint","INTERSECT",VERTEX,{"derivedFrom":[subQ1,subQ0]});Q78=makeQuery(id+"F0.imprint","IMPRINT",FACE,{"disambiguationData":[TD([[makeQuery(id+"F0.imprint","IMPRINT",EDGE,{"disambiguationData":[TD([[subQ2,-1.0]])],"derivedFrom":subQ1}),-1.0]])]});}
            var Q79;
            {var subQ0=sQuery(id+"F0.wireOp",EDGE,"E39");var subQ1=sQuery(id+"F0.wireOp",EDGE,"E6");var subQ2=makeQuery(id+"F0.imprint","INTERSECT",VERTEX,{"derivedFrom":[subQ1,subQ0]});Q79=makeQuery(id+"F0.imprint","IMPRINT",FACE,{"disambiguationData":[TD([[makeQuery(id+"F0.imprint","IMPRINT",EDGE,{"disambiguationData":[TD([[subQ2,-1.0]])],"derivedFrom":subQ0}),-1.0]])]});}
            var Q80;
            {var subQ5=sQuery(id+"F0.wireOp",EDGE,"E39");var subQ6=sQuery(id+"F0.wireOp",EDGE,"E6");var subQ7=makeQuery(id+"F0.imprint","INTERSECT",VERTEX,{"derivedFrom":[subQ6,subQ5]});Q80=makeQuery(id+"F0.imprint","IMPRINT",FACE,{"disambiguationData":[TD([[makeQuery(id+"F0.imprint","IMPRINT",EDGE,{"disambiguationData":[TD([[subQ7,1.0]])],"derivedFrom":subQ5}),-1.0]])]});}
            var Q81;
            {var subQ0=sQuery(id+"F0.wireOp",EDGE,"E39");var subQ1=sQuery(id+"F0.wireOp",EDGE,"E19.MirrorCS");var subQ2=makeQuery(id+"F0.imprint","INTERSECT",VERTEX,{"derivedFrom":[subQ1,subQ0]});Q81=makeQuery(id+"F0.imprint","IMPRINT",FACE,{"disambiguationData":[TD([[makeQuery(id+"F0.imprint","IMPRINT",EDGE,{"disambiguationData":[TD([[subQ2,-1.0]])],"derivedFrom":subQ1}),-1.0]])]});}
            var Q82;
            {var subQ0=sQuery(id+"F0.wireOp",EDGE,"E39");var subQ1=sQuery(id+"F0.wireOp",EDGE,"E1");var subQ2=makeQuery(id+"F0.imprint","INTERSECT",VERTEX,{"derivedFrom":[subQ1,subQ0]});Q82=makeQuery(id+"F0.imprint","IMPRINT",FACE,{"disambiguationData":[TD([[makeQuery(id+"F0.imprint","IMPRINT",EDGE,{"disambiguationData":[TD([[subQ2,-1.0]])],"derivedFrom":subQ0}),-1.0]])]});}
            var Q83;
            {var subQ5=sQuery(id+"F0.wireOp",EDGE,"E39");var subQ6=sQuery(id+"F0.wireOp",EDGE,"E1");var subQ7=makeQuery(id+"F0.imprint","INTERSECT",VERTEX,{"derivedFrom":[subQ6,subQ5]});Q83=makeQuery(id+"F0.imprint","IMPRINT",FACE,{"disambiguationData":[TD([[makeQuery(id+"F0.imprint","IMPRINT",EDGE,{"disambiguationData":[TD([[subQ7,1.0]])],"derivedFrom":subQ5}),-1.0]])]});}
            var Q84;
            {var subQ0=sQuery(id+"F0.wireOp",EDGE,"E39");var subQ1=sQuery(id+"F0.wireOp",EDGE,"E17.MirrorCS");var subQ2=makeQuery(id+"F0.imprint","INTERSECT",VERTEX,{"derivedFrom":[subQ1,subQ0]});Q84=makeQuery(id+"F0.imprint","IMPRINT",FACE,{"disambiguationData":[TD([[makeQuery(id+"F0.imprint","IMPRINT",EDGE,{"disambiguationData":[TD([[subQ2,-1.0]])],"derivedFrom":subQ1}),-1.0]])]});}
            var Q85;
            {var subQ0=sQuery(id+"F0.wireOp",EDGE,"E39");var subQ1=sQuery(id+"F0.wireOp",EDGE,"E4");var subQ2=makeQuery(id+"F0.imprint","INTERSECT",VERTEX,{"derivedFrom":[subQ1,subQ0]});Q85=makeQuery(id+"F0.imprint","IMPRINT",FACE,{"disambiguationData":[TD([[makeQuery(id+"F0.imprint","IMPRINT",EDGE,{"disambiguationData":[TD([[subQ2,-1.0]])],"derivedFrom":subQ0}),-1.0]])]});}
            var Q86;
            {var subQ0=sQuery(id+"F0.wireOp",EDGE,"E39");var subQ1=sQuery(id+"F0.wireOp",EDGE,"E4");var subQ2=makeQuery(id+"F0.imprint","INTERSECT",VERTEX,{"derivedFrom":[subQ1,subQ0]});Q86=makeQuery(id+"F0.imprint","IMPRINT",FACE,{"disambiguationData":[TD([[makeQuery(id+"F0.imprint","IMPRINT",EDGE,{"disambiguationData":[TD([[subQ2,1.0]])],"derivedFrom":subQ0}),-1.0]])]});}
            var Q87;
            {var subQ0=sQuery(id+"F0.wireOp",EDGE,"E39");var subQ1=sQuery(id+"F0.wireOp",EDGE,"E15");var subQ2=makeQuery(id+"F0.imprint","INTERSECT",VERTEX,{"derivedFrom":[subQ1,subQ0]});Q87=makeQuery(id+"F0.imprint","IMPRINT",FACE,{"disambiguationData":[TD([[makeQuery(id+"F0.imprint","IMPRINT",EDGE,{"disambiguationData":[TD([[subQ2,-1.0]])],"derivedFrom":subQ1}),-1.0]])]});}
            var Q88;
            {var subQ0=sQuery(id+"F0.wireOp",EDGE,"E39");var subQ1=sQuery(id+"F0.wireOp",EDGE,"E14");var subQ2=makeQuery(id+"F0.imprint","INTERSECT",VERTEX,{"derivedFrom":[subQ1,subQ0]});Q88=makeQuery(id+"F0.imprint","IMPRINT",FACE,{"disambiguationData":[TD([[makeQuery(id+"F0.imprint","IMPRINT",EDGE,{"disambiguationData":[TD([[subQ2,1.0]])],"derivedFrom":subQ1}),-1.0]])]});}
            var Q89;
            {var subQ0=sQuery(id+"F0.wireOp",EDGE,"E39");var subQ1=sQuery(id+"F0.wireOp",EDGE,"E21.MirrorCS");var subQ2=makeQuery(id+"F0.imprint","INTERSECT",VERTEX,{"derivedFrom":[subQ1,subQ0]});Q89=makeQuery(id+"F0.imprint","IMPRINT",FACE,{"disambiguationData":[TD([[makeQuery(id+"F0.imprint","IMPRINT",EDGE,{"disambiguationData":[TD([[subQ2,1.0]])],"derivedFrom":subQ1}),1.0]])]});}
            var Q90;
            {var subQ0=sQuery(id+"F0.wireOp",EDGE,"E39");var subQ1=sQuery(id+"F0.wireOp",EDGE,"E21.MirrorCS");var subQ2=makeQuery(id+"F0.imprint","INTERSECT",VERTEX,{"derivedFrom":[subQ1,subQ0]});Q90=makeQuery(id+"F0.imprint","IMPRINT",FACE,{"disambiguationData":[TD([[makeQuery(id+"F0.imprint","IMPRINT",EDGE,{"disambiguationData":[TD([[subQ2,1.0]])],"derivedFrom":subQ1}),-1.0]])]});}
            var Q91;
            {var subQ0=sQuery(id+"F0.wireOp",EDGE,"E39");var subQ1=sQuery(id+"F0.wireOp",EDGE,"E20.MirrorCS");var subQ2=makeQuery(id+"F0.imprint","INTERSECT",VERTEX,{"derivedFrom":[subQ1,subQ0]});Q91=makeQuery(id+"F0.imprint","IMPRINT",FACE,{"disambiguationData":[TD([[makeQuery(id+"F0.imprint","IMPRINT",EDGE,{"disambiguationData":[TD([[subQ2,1.0]])],"derivedFrom":subQ1}),-1.0]])]});}
            var Q92;
            {var subQ0=sQuery(id+"F0.wireOp",EDGE,"E39");var subQ1=sQuery(id+"F0.wireOp",EDGE,"E19.MirrorCS");var subQ2=makeQuery(id+"F0.imprint","INTERSECT",VERTEX,{"derivedFrom":[subQ1,subQ0]});Q92=makeQuery(id+"F0.imprint","IMPRINT",FACE,{"disambiguationData":[TD([[makeQuery(id+"F0.imprint","IMPRINT",EDGE,{"disambiguationData":[TD([[subQ2,1.0]])],"derivedFrom":subQ1}),1.0]])]});}
            var Q93;
            {var subQ0=sQuery(id+"F0.wireOp",EDGE,"E39");var subQ1=sQuery(id+"F0.wireOp",EDGE,"E19.MirrorCS");var subQ2=makeQuery(id+"F0.imprint","INTERSECT",VERTEX,{"derivedFrom":[subQ1,subQ0]});Q93=makeQuery(id+"F0.imprint","IMPRINT",FACE,{"disambiguationData":[TD([[makeQuery(id+"F0.imprint","IMPRINT",EDGE,{"disambiguationData":[TD([[subQ2,1.0]])],"derivedFrom":subQ1}),-1.0]])]});}
            var Q94;
            {var subQ0=sQuery(id+"F0.wireOp",EDGE,"E39");var subQ1=sQuery(id+"F0.wireOp",EDGE,"E18.MirrorCS");var subQ2=makeQuery(id+"F0.imprint","INTERSECT",VERTEX,{"derivedFrom":[subQ1,subQ0]});Q94=makeQuery(id+"F0.imprint","IMPRINT",FACE,{"disambiguationData":[TD([[makeQuery(id+"F0.imprint","IMPRINT",EDGE,{"disambiguationData":[TD([[subQ2,1.0]])],"derivedFrom":subQ1}),-1.0]])]});}
            var Q95;
            {var subQ0=sQuery(id+"F0.wireOp",EDGE,"E39");var subQ1=sQuery(id+"F0.wireOp",EDGE,"E17.MirrorCS");var subQ2=makeQuery(id+"F0.imprint","INTERSECT",VERTEX,{"derivedFrom":[subQ1,subQ0]});Q95=makeQuery(id+"F0.imprint","IMPRINT",FACE,{"disambiguationData":[TD([[makeQuery(id+"F0.imprint","IMPRINT",EDGE,{"disambiguationData":[TD([[subQ2,1.0]])],"derivedFrom":subQ1}),1.0]])]});}
            var Q96;
            {var subQ0=sQuery(id+"F0.wireOp",EDGE,"E39");var subQ1=sQuery(id+"F0.wireOp",EDGE,"E17.MirrorCS");var subQ2=makeQuery(id+"F0.imprint","INTERSECT",VERTEX,{"derivedFrom":[subQ1,subQ0]});Q96=makeQuery(id+"F0.imprint","IMPRINT",FACE,{"disambiguationData":[TD([[makeQuery(id+"F0.imprint","IMPRINT",EDGE,{"disambiguationData":[TD([[subQ2,1.0]])],"derivedFrom":subQ1}),-1.0]])]});}
            var Q97;
            {var subQ0=sQuery(id+"F0.wireOp",EDGE,"E39");var subQ1=sQuery(id+"F0.wireOp",EDGE,"E16.MirrorCS");var subQ2=makeQuery(id+"F0.imprint","INTERSECT",VERTEX,{"derivedFrom":[subQ1,subQ0]});Q97=makeQuery(id+"F0.imprint","IMPRINT",FACE,{"disambiguationData":[TD([[makeQuery(id+"F0.imprint","IMPRINT",EDGE,{"disambiguationData":[TD([[subQ2,1.0]])],"derivedFrom":subQ1}),-1.0]])]});}
            var Q98;
            {var subQ0=sQuery(id+"F0.wireOp",EDGE,"E39");var subQ1=sQuery(id+"F0.wireOp",EDGE,"E15");var subQ2=makeQuery(id+"F0.imprint","INTERSECT",VERTEX,{"derivedFrom":[subQ1,subQ0]});Q98=makeQuery(id+"F0.imprint","IMPRINT",FACE,{"disambiguationData":[TD([[makeQuery(id+"F0.imprint","IMPRINT",EDGE,{"disambiguationData":[TD([[subQ2,1.0]])],"derivedFrom":subQ1}),1.0]])]});}
            var Q99;
            {var subQ0=sQuery(id+"F0.wireOp",EDGE,"E39");var subQ1=sQuery(id+"F0.wireOp",EDGE,"E15");var subQ2=makeQuery(id+"F0.imprint","INTERSECT",VERTEX,{"derivedFrom":[subQ1,subQ0]});Q99=makeQuery(id+"F0.imprint","IMPRINT",FACE,{"disambiguationData":[TD([[makeQuery(id+"F0.imprint","IMPRINT",EDGE,{"disambiguationData":[TD([[subQ2,1.0]])],"derivedFrom":subQ1}),-1.0]])]});}
            var Q100;
            {var subQ0=sQuery(id+"F0.wireOp",EDGE,"E48");var subQ1=sQuery(id+"F0.wireOp",EDGE,"E21.MirrorCS");var subQ2=makeQuery(id+"F0.imprint","INTERSECT",VERTEX,{"derivedFrom":[subQ1,subQ0]});Q100=makeQuery(id+"F0.imprint","IMPRINT",FACE,{"disambiguationData":[TD([[makeQuery(id+"F0.imprint","IMPRINT",EDGE,{"disambiguationData":[TD([[subQ2,-1.0]])],"derivedFrom":subQ1}),-1.0]])]});}
            var Q101;
            {var subQ0=sQuery(id+"F0.wireOp",EDGE,"E48");var subQ1=sQuery(id+"F0.wireOp",EDGE,"E21.MirrorCS");var subQ2=makeQuery(id+"F0.imprint","INTERSECT",VERTEX,{"derivedFrom":[subQ1,subQ0]});Q101=makeQuery(id+"F0.imprint","IMPRINT",FACE,{"disambiguationData":[TD([[makeQuery(id+"F0.imprint","IMPRINT",EDGE,{"disambiguationData":[TD([[subQ2,-1.0]])],"derivedFrom":subQ1}),1.0]])]});}
            var Q102;
            {var subQ0=sQuery(id+"F0.wireOp",EDGE,"E48");var subQ1=sQuery(id+"F0.wireOp",EDGE,"E14");var subQ2=makeQuery(id+"F0.imprint","INTERSECT",VERTEX,{"derivedFrom":[subQ1,subQ0]});Q102=makeQuery(id+"F0.imprint","IMPRINT",FACE,{"disambiguationData":[TD([[makeQuery(id+"F0.imprint","IMPRINT",EDGE,{"disambiguationData":[TD([[subQ2,-1.0]])],"derivedFrom":subQ1}),-1.0]])]});}
            var Q103;
            {var subQ0=sQuery(id+"F0.wireOp",EDGE,"E48");var subQ1=sQuery(id+"F0.wireOp",EDGE,"E15");var subQ2=makeQuery(id+"F0.imprint","INTERSECT",VERTEX,{"derivedFrom":[subQ1,subQ0]});Q103=makeQuery(id+"F0.imprint","IMPRINT",FACE,{"disambiguationData":[TD([[makeQuery(id+"F0.imprint","IMPRINT",EDGE,{"disambiguationData":[TD([[subQ2,-1.0]])],"derivedFrom":subQ1}),-1.0]])]});}
            var Q104;
            {var subQ0=sQuery(id+"F0.wireOp",EDGE,"E48");var subQ1=sQuery(id+"F0.wireOp",EDGE,"E15");var subQ2=makeQuery(id+"F0.imprint","INTERSECT",VERTEX,{"derivedFrom":[subQ1,subQ0]});Q104=makeQuery(id+"F0.imprint","IMPRINT",FACE,{"disambiguationData":[TD([[makeQuery(id+"F0.imprint","IMPRINT",EDGE,{"disambiguationData":[TD([[subQ2,-1.0]])],"derivedFrom":subQ1}),1.0]])]});}
            var Q105;
            {var subQ0=sQuery(id+"F0.wireOp",EDGE,"E48");var subQ1=sQuery(id+"F0.wireOp",EDGE,"E16.MirrorCS");var subQ2=makeQuery(id+"F0.imprint","INTERSECT",VERTEX,{"derivedFrom":[subQ1,subQ0]});Q105=makeQuery(id+"F0.imprint","IMPRINT",FACE,{"disambiguationData":[TD([[makeQuery(id+"F0.imprint","IMPRINT",EDGE,{"disambiguationData":[TD([[subQ2,-1.0]])],"derivedFrom":subQ1}),-1.0]])]});}
            var Q106;
            {var subQ0=sQuery(id+"F0.wireOp",EDGE,"E48");var subQ1=sQuery(id+"F0.wireOp",EDGE,"E17.MirrorCS");var subQ2=makeQuery(id+"F0.imprint","INTERSECT",VERTEX,{"derivedFrom":[subQ1,subQ0]});Q106=makeQuery(id+"F0.imprint","IMPRINT",FACE,{"disambiguationData":[TD([[makeQuery(id+"F0.imprint","IMPRINT",EDGE,{"disambiguationData":[TD([[subQ2,-1.0]])],"derivedFrom":subQ1}),-1.0]])]});}
            var Q107;
            {var subQ0=sQuery(id+"F0.wireOp",EDGE,"E48");var subQ1=sQuery(id+"F0.wireOp",EDGE,"E17.MirrorCS");var subQ2=makeQuery(id+"F0.imprint","INTERSECT",VERTEX,{"derivedFrom":[subQ1,subQ0]});Q107=makeQuery(id+"F0.imprint","IMPRINT",FACE,{"disambiguationData":[TD([[makeQuery(id+"F0.imprint","IMPRINT",EDGE,{"disambiguationData":[TD([[subQ2,-1.0]])],"derivedFrom":subQ1}),1.0]])]});}
            var Q108;
            {var subQ0=sQuery(id+"F0.wireOp",EDGE,"E48");var subQ1=sQuery(id+"F0.wireOp",EDGE,"E18.MirrorCS");var subQ2=makeQuery(id+"F0.imprint","INTERSECT",VERTEX,{"derivedFrom":[subQ1,subQ0]});Q108=makeQuery(id+"F0.imprint","IMPRINT",FACE,{"disambiguationData":[TD([[makeQuery(id+"F0.imprint","IMPRINT",EDGE,{"disambiguationData":[TD([[subQ2,-1.0]])],"derivedFrom":subQ1}),-1.0]])]});}
            var Q109;
            {var subQ0=sQuery(id+"F0.wireOp",EDGE,"E48");var subQ1=sQuery(id+"F0.wireOp",EDGE,"E19.MirrorCS");var subQ2=makeQuery(id+"F0.imprint","INTERSECT",VERTEX,{"derivedFrom":[subQ1,subQ0]});Q109=makeQuery(id+"F0.imprint","IMPRINT",FACE,{"disambiguationData":[TD([[makeQuery(id+"F0.imprint","IMPRINT",EDGE,{"disambiguationData":[TD([[subQ2,-1.0]])],"derivedFrom":subQ1}),-1.0]])]});}
            var Q110;
            {var subQ0=sQuery(id+"F0.wireOp",EDGE,"E48");var subQ1=sQuery(id+"F0.wireOp",EDGE,"E19.MirrorCS");var subQ2=makeQuery(id+"F0.imprint","INTERSECT",VERTEX,{"derivedFrom":[subQ1,subQ0]});Q110=makeQuery(id+"F0.imprint","IMPRINT",FACE,{"disambiguationData":[TD([[makeQuery(id+"F0.imprint","IMPRINT",EDGE,{"disambiguationData":[TD([[subQ2,-1.0]])],"derivedFrom":subQ1}),1.0]])]});}
            var Q111;
            {var subQ0=sQuery(id+"F0.wireOp",EDGE,"E48");var subQ1=sQuery(id+"F0.wireOp",EDGE,"E20.MirrorCS");var subQ2=makeQuery(id+"F0.imprint","INTERSECT",VERTEX,{"derivedFrom":[subQ1,subQ0]});Q111=makeQuery(id+"F0.imprint","IMPRINT",FACE,{"disambiguationData":[TD([[makeQuery(id+"F0.imprint","IMPRINT",EDGE,{"disambiguationData":[TD([[subQ2,-1.0]])],"derivedFrom":subQ1}),-1.0]])]});}
            var Q112;
            {var subQ0=sQuery(id+"F0.wireOp",EDGE,"E40.0");var subQ1=sQuery(id+"F0.wireOp",EDGE,"E21.MirrorCS");var subQ2=makeQuery(id+"F0.imprint","INTERSECT",VERTEX,{"derivedFrom":[subQ1,subQ0]});Q112=makeQuery(id+"F0.imprint","IMPRINT",FACE,{"disambiguationData":[TD([[makeQuery(id+"F0.imprint","IMPRINT",EDGE,{"disambiguationData":[TD([[subQ2,1.0]])],"derivedFrom":subQ1}),1.0]])]});}
            var Q113;
            {var subQ0=sQuery(id+"F0.wireOp",EDGE,"E40.0");var subQ1=sQuery(id+"F0.wireOp",EDGE,"E19.MirrorCS");var subQ2=makeQuery(id+"F0.imprint","INTERSECT",VERTEX,{"derivedFrom":[subQ1,subQ0]});Q113=makeQuery(id+"F0.imprint","IMPRINT",FACE,{"disambiguationData":[TD([[makeQuery(id+"F0.imprint","IMPRINT",EDGE,{"disambiguationData":[TD([[subQ2,1.0]])],"derivedFrom":subQ1}),1.0]])]});}
            var Q114;
            {var subQ0=sQuery(id+"F0.wireOp",EDGE,"E40.0");var subQ1=sQuery(id+"F0.wireOp",EDGE,"E17.MirrorCS");var subQ2=makeQuery(id+"F0.imprint","INTERSECT",VERTEX,{"derivedFrom":[subQ1,subQ0]});Q114=makeQuery(id+"F0.imprint","IMPRINT",FACE,{"disambiguationData":[TD([[makeQuery(id+"F0.imprint","IMPRINT",EDGE,{"disambiguationData":[TD([[subQ2,1.0]])],"derivedFrom":subQ1}),1.0]])]});}
            var Q115;
            {var subQ0=sQuery(id+"F0.wireOp",EDGE,"E40.0");var subQ1=sQuery(id+"F0.wireOp",EDGE,"E15");var subQ2=makeQuery(id+"F0.imprint","INTERSECT",VERTEX,{"derivedFrom":[subQ1,subQ0]});Q115=makeQuery(id+"F0.imprint","IMPRINT",FACE,{"disambiguationData":[TD([[makeQuery(id+"F0.imprint","IMPRINT",EDGE,{"disambiguationData":[TD([[subQ2,1.0]])],"derivedFrom":subQ1}),1.0]])]});}
            var Q116;
            {var subQ0=sQuery(id+"F0.wireOp",EDGE,"E38");var subQ1=sQuery(id+"F0.wireOp",EDGE,"E1");var subQ2=makeQuery(id+"F0.imprint","INTERSECT",VERTEX,{"derivedFrom":[subQ1,subQ0]});Q116=makeQuery(id+"F0.imprint","IMPRINT",FACE,{"disambiguationData":[TD([[makeQuery(id+"F0.imprint","IMPRINT",EDGE,{"disambiguationData":[TD([[subQ2,-1.0]])],"derivedFrom":subQ1}),1.0]])]});}
            var Q117;
            {var subQ0=sQuery(id+"F0.wireOp",EDGE,"E38");var subQ1=sQuery(id+"F0.wireOp",EDGE,"E1");var subQ2=makeQuery(id+"F0.imprint","INTERSECT",VERTEX,{"derivedFrom":[subQ1,subQ0]});Q117=makeQuery(id+"F0.imprint","IMPRINT",FACE,{"disambiguationData":[TD([[makeQuery(id+"F0.imprint","IMPRINT",EDGE,{"disambiguationData":[TD([[subQ2,-1.0]])],"derivedFrom":subQ1}),-1.0]])]});}
            var Q118;
            {var subQ0=sQuery(id+"F0.wireOp",EDGE,"E48");var subQ1=sQuery(id+"F0.wireOp",EDGE,"E4");var subQ2=makeQuery(id+"F0.imprint","INTERSECT",VERTEX,{"derivedFrom":[subQ1,subQ0]});Q118=makeQuery(id+"F0.imprint","IMPRINT",FACE,{"disambiguationData":[TD([[makeQuery(id+"F0.imprint","IMPRINT",EDGE,{"disambiguationData":[TD([[subQ2,-1.0]])],"derivedFrom":subQ1}),1.0]])]});}
            var Q119;
            {var subQ0=sQuery(id+"F0.wireOp",EDGE,"E48");var subQ1=sQuery(id+"F0.wireOp",EDGE,"E4");var subQ2=makeQuery(id+"F0.imprint","INTERSECT",VERTEX,{"derivedFrom":[subQ1,subQ0]});Q119=makeQuery(id+"F0.imprint","IMPRINT",FACE,{"disambiguationData":[TD([[makeQuery(id+"F0.imprint","IMPRINT",EDGE,{"disambiguationData":[TD([[subQ2,-1.0]])],"derivedFrom":subQ1}),-1.0]])]});}
            extrude(context, id + "F1", {"entities" : qUnion([Q0, Q1, Q2, Q3, Q4, Q5, Q6, Q7, Q8, Q9, Q10, Q11, Q12, Q13, Q14, Q15, Q16, Q17, Q18, Q19, Q20, Q21, Q22, Q23, Q24, Q25, Q26, Q27, Q28, Q29, Q30, Q31, Q32, Q33, Q34, Q35, Q36, Q37, Q38, Q39, Q40, Q41, Q42, Q43, Q44, Q45, Q46, Q47, Q48, Q49, Q50, Q51, Q52, Q53, Q54, Q55, Q56, Q57, Q58, Q59, Q60, Q61, Q62, Q63, Q64, Q65, Q66, Q67, Q68, Q69, Q70, Q71, Q72, Q73, Q74, Q75, Q76, Q77, Q78, Q79, Q80, Q81, Q82, Q83, Q84, Q85, Q86, Q87, Q88, Q89, Q90, Q91, Q92, Q93, Q94, Q95, Q96, Q97, Q98, Q99, Q100, Q101, Q102, Q103, Q104, Q105, Q106, Q107, Q108, Q109, Q110, Q111, Q112, Q113, Q114, Q115, Q116, Q117, Q118, Q119]), "depth" : 6.35 * mm, "offsetDistance" : 25.4 * mm});
        }
        {
            var Q0;
            Q0=makeQuery(id+"F1.opExtrude","CAP_EDGE",EDGE,{"disambiguationData":[OSD([sQuery(id+"F0.wireOp",EDGE,"E8"),sQuery(id+"F0.wireOp",EDGE,"E9"),sQuery(id+"F0.wireOp",EDGE,"E10"),sQuery(id+"F0.wireOp",EDGE,"E11")])],"isStart":false});
            var Q1;
            Q1=makeQuery(id+"F1.opExtrude","CAP_EDGE",EDGE,{"disambiguationData":[OSD([sQuery(id+"F0.wireOp",EDGE,"E8"),sQuery(id+"F0.wireOp",EDGE,"E9"),sQuery(id+"F0.wireOp",EDGE,"E10"),sQuery(id+"F0.wireOp",EDGE,"E11")])],"isStart":true});
            fillet(context, id + "F2", {"entities" : qUnion([Q0, Q1]), "radius" : 2.54 * mm, "tangentPropagation" : true, "allowEdgeOverflow" : false});
        }
    });
